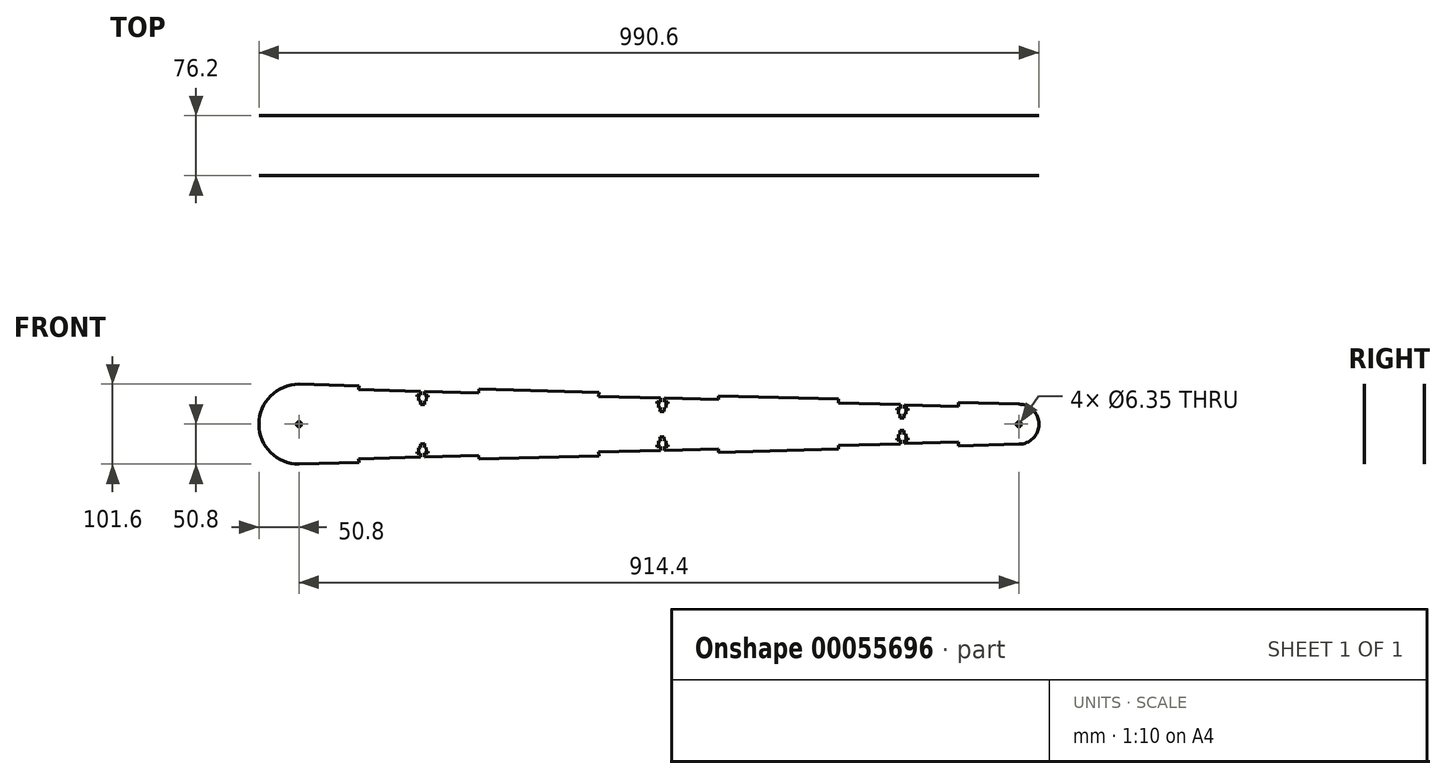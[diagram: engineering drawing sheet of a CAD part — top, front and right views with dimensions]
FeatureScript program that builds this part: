
annotation { "Feature Type Name" : "Feature", "Feature Type Description" : "" }
export const myFeature = defineFeature(function(context is Context, id is Id, definition is map)
    precondition{}
    {
        {
            assignVariable(context, id + "F0", {"name" : "thick", "anyValue" : .188});
        }
        {
            var Q0;
            Q0=qCreatedBy(makeId("Front.planeOp"),FACE);
            var sketch = newSketch(context, id + "F1", { "sketchPlane" : qUnion([Q0])});
            skLineSegment(sketch, "E0", {"start": v(0, 50.8) * mm, "end": v(914.4, 25.4) * mm});
            skLineSegment(sketch, "E1", {"start": v(0, -50.8) * mm, "end": v(914.4, -25.4) * mm});
            skArc(sketch, "E2", {"start": v(0, 50.8) * mm, "mid": v(-50.8, 0) * mm, "end": v(0, -50.8) * mm});
            skLineSegment(sketch, "E3", {"start": v(0, 0) * mm, "end": v(914.4, 0) * mm, "construction": true});
            skArc(sketch, "E4", {"start": v(914.4, 25.4) * mm, "mid": v(939.8, 0) * mm, "end": v(914.4, -25.4) * mm});
            skLineSegment(sketch, "E5", {"start": v(76.17, 48.68) * mm, "end": v(76.04, 43.91) * mm});
            skLineSegment(sketch, "E6", {"start": v(76.04, 43.91) * mm, "end": v(228.38, 39.68) * mm});
            skLineSegment(sketch, "E7", {"start": v(228.38, 39.68) * mm, "end": v(228.51, 44.45) * mm});
            skLineSegment(sketch, "E8", {"start": v(76.17, -48.68) * mm, "end": v(76.04, -43.91) * mm});
            skLineSegment(sketch, "E9", {"start": v(76.04, -43.91) * mm, "end": v(228.38, -39.68) * mm});
            skLineSegment(sketch, "E10", {"start": v(228.38, -39.68) * mm, "end": v(228.51, -44.45) * mm});
            skCircle(sketch, "E11", {"center": v(0, 0) * mm, "radius": 3.17 * mm});
            skCircle(sketch, "E12", {"center": v(914.4, 0) * mm, "radius": 3.18 * mm});
            skLineSegment(sketch, "E13", {"start": v(157.22, 41.66) * mm, "end": v(156.06, 0) * mm, "construction": true});
            skLineSegment(sketch, "E14", {"start": v(154.67, 41.73) * mm, "end": v(154.54, 36.95) * mm});
            skLineSegment(sketch, "E15", {"start": v(154.54, 36.95) * mm, "end": v(150.1, 37.08) * mm});
            skLineSegment(sketch, "E16", {"start": v(150.1, 37.08) * mm, "end": v(150.05, 35.05) * mm});
            skLineSegment(sketch, "E17", {"start": v(150.05, 35.05) * mm, "end": v(152.27, 34.98) * mm});
            skLineSegment(sketch, "E18", {"start": v(152.27, 34.98) * mm, "end": v(152.13, 29.9) * mm});
            skLineSegment(sketch, "E19", {"start": v(152.13, 29.9) * mm, "end": v(154.34, 29.84) * mm});
            skLineSegment(sketch, "E20", {"start": v(154.34, 29.84) * mm, "end": v(154.2, 24.92) * mm});
            skLineSegment(sketch, "E21", {"start": v(154.2, 24.92) * mm, "end": v(156.75, 24.85) * mm});
            skLineSegment(sketch, "E22.MirrorCS", {"start": v(159.77, 41.58) * mm, "end": v(159.64, 36.81) * mm});
            skLineSegment(sketch, "E23.MirrorCS", {"start": v(159.64, 36.81) * mm, "end": v(164.07, 36.69) * mm});
            skLineSegment(sketch, "E24.MirrorCS", {"start": v(164.07, 36.69) * mm, "end": v(164.02, 34.66) * mm});
            skLineSegment(sketch, "E25.MirrorCS", {"start": v(164.02, 34.66) * mm, "end": v(161.8, 34.72) * mm});
            skLineSegment(sketch, "E26.MirrorCS", {"start": v(161.8, 34.72) * mm, "end": v(161.65, 29.64) * mm});
            skLineSegment(sketch, "E27.MirrorCS", {"start": v(161.65, 29.64) * mm, "end": v(159.44, 29.7) * mm});
            skLineSegment(sketch, "E28.MirrorCS", {"start": v(159.44, 29.7) * mm, "end": v(159.3, 24.78) * mm});
            skLineSegment(sketch, "E29.MirrorCS", {"start": v(159.3, 24.78) * mm, "end": v(156.75, 24.85) * mm});
            skLineSegment(sketch, "E30", {"start": v(76.04, -43.91) * mm, "end": v(228.38, 39.68) * mm, "construction": true});
            skLineSegment(sketch, "E31", {"start": v(228.38, -39.68) * mm, "end": v(76.04, 43.91) * mm, "construction": true});
            skLineSegment(sketch, "E32.MirrorCS", {"start": v(159.64, -36.81) * mm, "end": v(164.07, -36.69) * mm});
            skLineSegment(sketch, "E33.MirrorCS", {"start": v(161.65, -29.64) * mm, "end": v(159.44, -29.7) * mm});
            skLineSegment(sketch, "E34.MirrorCS", {"start": v(152.13, -29.9) * mm, "end": v(154.34, -29.84) * mm});
            skLineSegment(sketch, "E35.MirrorCS", {"start": v(159.3, -24.78) * mm, "end": v(156.75, -24.85) * mm});
            skLineSegment(sketch, "E36.MirrorCS", {"start": v(154.2, -24.92) * mm, "end": v(156.75, -24.85) * mm});
            skLineSegment(sketch, "E37.MirrorCS", {"start": v(154.54, -36.95) * mm, "end": v(150.1, -37.08) * mm});
            skLineSegment(sketch, "E38.MirrorCS", {"start": v(164.07, -36.69) * mm, "end": v(164.02, -34.66) * mm});
            skLineSegment(sketch, "E39.MirrorCS", {"start": v(154.34, -29.84) * mm, "end": v(154.2, -24.92) * mm});
            skLineSegment(sketch, "E40.MirrorCS", {"start": v(161.8, -34.72) * mm, "end": v(161.65, -29.64) * mm});
            skLineSegment(sketch, "E41.MirrorCS", {"start": v(150.1, -37.08) * mm, "end": v(150.05, -35.05) * mm});
            skLineSegment(sketch, "E42.MirrorCS", {"start": v(159.77, -41.58) * mm, "end": v(159.64, -36.81) * mm});
            skLineSegment(sketch, "E43.MirrorCS", {"start": v(159.44, -29.7) * mm, "end": v(159.3, -24.78) * mm});
            skLineSegment(sketch, "E44.MirrorCS", {"start": v(152.27, -34.98) * mm, "end": v(152.13, -29.9) * mm});
            skLineSegment(sketch, "E45.MirrorCS", {"start": v(154.67, -41.73) * mm, "end": v(154.54, -36.95) * mm});
            skLineSegment(sketch, "E46.1.0.0", {"start": v(380.72, 35.45) * mm, "end": v(533.06, 31.22) * mm});
            skLineSegment(sketch, "E46.1.0.1", {"start": v(380.85, 40.22) * mm, "end": v(380.72, 35.45) * mm});
            skLineSegment(sketch, "E46.1.0.2", {"start": v(464.46, 33.12) * mm, "end": v(464.32, 28.35) * mm});
            skLineSegment(sketch, "E46.1.0.3", {"start": v(466.48, 26.26) * mm, "end": v(466.33, 21.18) * mm});
            skLineSegment(sketch, "E46.1.0.4", {"start": v(459.35, 33.26) * mm, "end": v(459.22, 28.49) * mm});
            skLineSegment(sketch, "E46.1.0.5", {"start": v(464.13, 21.24) * mm, "end": v(463.99, 16.31) * mm});
            skLineSegment(sketch, "E46.1.0.6", {"start": v(533.06, 31.22) * mm, "end": v(533.2, 35.99) * mm});
            skLineSegment(sketch, "E46.1.0.7", {"start": v(459.02, 21.38) * mm, "end": v(458.89, 16.45) * mm});
            skLineSegment(sketch, "E46.1.0.8", {"start": v(463.99, 16.31) * mm, "end": v(461.44, 16.38) * mm});
            skLineSegment(sketch, "E46.1.0.9", {"start": v(456.81, 21.44) * mm, "end": v(459.02, 21.38) * mm});
            skLineSegment(sketch, "E46.1.0.10", {"start": v(464.32, 28.35) * mm, "end": v(468.75, 28.22) * mm});
            skLineSegment(sketch, "E46.1.0.11", {"start": v(466.33, 21.18) * mm, "end": v(464.13, 21.24) * mm});
            skLineSegment(sketch, "E46.1.0.12", {"start": v(456.95, 26.52) * mm, "end": v(456.81, 21.44) * mm});
            skLineSegment(sketch, "E46.1.0.13", {"start": v(458.89, 16.45) * mm, "end": v(461.44, 16.38) * mm});
            skLineSegment(sketch, "E46.1.0.14", {"start": v(468.7, 26.2) * mm, "end": v(466.48, 26.26) * mm});
            skLineSegment(sketch, "E46.1.0.15", {"start": v(468.75, 28.22) * mm, "end": v(468.7, 26.2) * mm});
            skLineSegment(sketch, "E46.1.0.16", {"start": v(459.22, 28.49) * mm, "end": v(454.79, 28.61) * mm});
            skLineSegment(sketch, "E46.1.0.17", {"start": v(454.79, 28.61) * mm, "end": v(454.73, 26.58) * mm});
            skLineSegment(sketch, "E46.2.0.0", {"start": v(685.4, 26.98) * mm, "end": v(837.74, 22.75) * mm});
            skLineSegment(sketch, "E46.2.0.1", {"start": v(685.54, 31.76) * mm, "end": v(685.4, 26.98) * mm});
            skLineSegment(sketch, "E46.2.0.2", {"start": v(769.14, 24.66) * mm, "end": v(769, 19.88) * mm});
            skLineSegment(sketch, "E46.2.0.3", {"start": v(771.16, 17.8) * mm, "end": v(771.02, 12.71) * mm});
            skLineSegment(sketch, "E46.2.0.4", {"start": v(764.04, 24.8) * mm, "end": v(763.9, 20.03) * mm});
            skLineSegment(sketch, "E46.2.0.5", {"start": v(768.8, 12.78) * mm, "end": v(768.67, 7.85) * mm});
            skLineSegment(sketch, "E46.2.0.6", {"start": v(837.74, 22.75) * mm, "end": v(837.88, 27.53) * mm});
            skLineSegment(sketch, "E46.2.0.7", {"start": v(763.7, 12.92) * mm, "end": v(763.57, 8) * mm});
            skLineSegment(sketch, "E46.2.0.8", {"start": v(768.67, 7.85) * mm, "end": v(766.12, 7.92) * mm});
            skLineSegment(sketch, "E46.2.0.9", {"start": v(761.5, 12.98) * mm, "end": v(763.7, 12.92) * mm});
            skLineSegment(sketch, "E46.2.0.10", {"start": v(769, 19.88) * mm, "end": v(773.44, 19.76) * mm});
            skLineSegment(sketch, "E46.2.0.11", {"start": v(771.02, 12.71) * mm, "end": v(768.8, 12.78) * mm});
            skLineSegment(sketch, "E46.2.0.12", {"start": v(761.64, 18.06) * mm, "end": v(761.5, 12.98) * mm});
            skLineSegment(sketch, "E46.2.0.13", {"start": v(763.57, 8) * mm, "end": v(766.12, 7.92) * mm});
            skLineSegment(sketch, "E46.2.0.14", {"start": v(773.38, 17.73) * mm, "end": v(771.16, 17.8) * mm});
            skLineSegment(sketch, "E46.2.0.15", {"start": v(773.44, 19.76) * mm, "end": v(773.38, 17.73) * mm});
            skLineSegment(sketch, "E46.2.0.16", {"start": v(763.9, 20.03) * mm, "end": v(759.47, 20.15) * mm});
            skLineSegment(sketch, "E46.2.0.17", {"start": v(759.47, 20.15) * mm, "end": v(759.42, 18.12) * mm});
            skLineSegment(sketch, "E46.direction1", {"start": v(76.04, 43.91) * mm, "end": v(380.72, 35.45) * mm, "construction": true});
            skLineSegment(sketch, "E47.1.0.0", {"start": v(464.13, -21.24) * mm, "end": v(463.99, -16.31) * mm});
            skLineSegment(sketch, "E47.1.0.1", {"start": v(459.02, -21.38) * mm, "end": v(458.89, -16.45) * mm});
            skLineSegment(sketch, "E47.1.0.2", {"start": v(466.48, -26.26) * mm, "end": v(466.33, -21.18) * mm});
            skLineSegment(sketch, "E47.1.0.3", {"start": v(380.85, -40.22) * mm, "end": v(380.72, -35.45) * mm});
            skLineSegment(sketch, "E47.1.0.4", {"start": v(533.06, -31.22) * mm, "end": v(533.2, -35.99) * mm});
            skLineSegment(sketch, "E47.1.0.5", {"start": v(380.72, -35.45) * mm, "end": v(533.06, -31.22) * mm});
            skLineSegment(sketch, "E47.1.0.6", {"start": v(464.46, -33.12) * mm, "end": v(464.32, -28.35) * mm});
            skLineSegment(sketch, "E47.1.0.7", {"start": v(459.35, -33.26) * mm, "end": v(459.22, -28.49) * mm});
            skLineSegment(sketch, "E47.1.0.8", {"start": v(456.95, -26.52) * mm, "end": v(456.81, -21.44) * mm});
            skLineSegment(sketch, "E47.1.0.9", {"start": v(463.99, -16.31) * mm, "end": v(461.44, -16.38) * mm});
            skLineSegment(sketch, "E47.1.0.10", {"start": v(454.79, -28.61) * mm, "end": v(454.73, -26.58) * mm});
            skLineSegment(sketch, "E47.1.0.11", {"start": v(464.32, -28.35) * mm, "end": v(468.75, -28.22) * mm});
            skLineSegment(sketch, "E47.1.0.12", {"start": v(468.75, -28.22) * mm, "end": v(468.7, -26.2) * mm});
            skLineSegment(sketch, "E47.1.0.13", {"start": v(466.33, -21.18) * mm, "end": v(464.13, -21.24) * mm});
            skLineSegment(sketch, "E47.1.0.14", {"start": v(459.22, -28.49) * mm, "end": v(454.79, -28.61) * mm});
            skLineSegment(sketch, "E47.1.0.15", {"start": v(456.81, -21.44) * mm, "end": v(459.02, -21.38) * mm});
            skLineSegment(sketch, "E47.1.0.16", {"start": v(458.89, -16.45) * mm, "end": v(461.44, -16.38) * mm});
            skLineSegment(sketch, "E47.2.0.0", {"start": v(768.8, -12.78) * mm, "end": v(768.67, -7.85) * mm});
            skLineSegment(sketch, "E47.2.0.1", {"start": v(763.7, -12.92) * mm, "end": v(763.57, -8) * mm});
            skLineSegment(sketch, "E47.2.0.2", {"start": v(771.16, -17.8) * mm, "end": v(771.02, -12.71) * mm});
            skLineSegment(sketch, "E47.2.0.3", {"start": v(685.54, -31.76) * mm, "end": v(685.4, -26.98) * mm});
            skLineSegment(sketch, "E47.2.0.4", {"start": v(837.74, -22.75) * mm, "end": v(837.88, -27.53) * mm});
            skLineSegment(sketch, "E47.2.0.5", {"start": v(685.4, -26.98) * mm, "end": v(837.74, -22.75) * mm});
            skLineSegment(sketch, "E47.2.0.6", {"start": v(769.14, -24.66) * mm, "end": v(769, -19.88) * mm});
            skLineSegment(sketch, "E47.2.0.7", {"start": v(764.04, -24.8) * mm, "end": v(763.9, -20.03) * mm});
            skLineSegment(sketch, "E47.2.0.8", {"start": v(761.64, -18.06) * mm, "end": v(761.5, -12.98) * mm});
            skLineSegment(sketch, "E47.2.0.9", {"start": v(768.67, -7.85) * mm, "end": v(766.12, -7.92) * mm});
            skLineSegment(sketch, "E47.2.0.10", {"start": v(759.47, -20.15) * mm, "end": v(759.42, -18.12) * mm});
            skLineSegment(sketch, "E47.2.0.11", {"start": v(769, -19.88) * mm, "end": v(773.44, -19.76) * mm});
            skLineSegment(sketch, "E47.2.0.12", {"start": v(773.44, -19.76) * mm, "end": v(773.38, -17.73) * mm});
            skLineSegment(sketch, "E47.2.0.13", {"start": v(771.02, -12.71) * mm, "end": v(768.8, -12.78) * mm});
            skLineSegment(sketch, "E47.2.0.14", {"start": v(763.9, -20.03) * mm, "end": v(759.47, -20.15) * mm});
            skLineSegment(sketch, "E47.2.0.15", {"start": v(761.5, -12.98) * mm, "end": v(763.7, -12.92) * mm});
            skLineSegment(sketch, "E47.2.0.16", {"start": v(763.57, -8) * mm, "end": v(766.12, -7.92) * mm});
            skLineSegment(sketch, "E47.direction1", {"start": v(159.44, -29.7) * mm, "end": v(464.13, -21.24) * mm, "construction": true});
            skLineSegment(sketch, "E48", {"start": v(150.05, -35.05) * mm, "end": v(152.27, -34.98) * mm});
            skLineSegment(sketch, "E49", {"start": v(161.8, -34.72) * mm, "end": v(164.02, -34.66) * mm});
            skLineSegment(sketch, "E50", {"start": v(454.73, 26.58) * mm, "end": v(456.95, 26.52) * mm});
            skLineSegment(sketch, "E51", {"start": v(454.73, -26.58) * mm, "end": v(456.95, -26.52) * mm});
            skLineSegment(sketch, "E52", {"start": v(466.48, -26.26) * mm, "end": v(468.7, -26.2) * mm});
            skLineSegment(sketch, "E53", {"start": v(759.42, 18.12) * mm, "end": v(761.64, 18.06) * mm});
            skLineSegment(sketch, "E54", {"start": v(759.42, -18.12) * mm, "end": v(761.64, -18.06) * mm});
            skLineSegment(sketch, "E55", {"start": v(771.16, -17.8) * mm, "end": v(773.38, -17.73) * mm});
            skSolve(sketch);
        }
        {
            var Q0;
            Q0=qCreatedBy(makeId("Front.planeOp"),FACE);
            cPlane(context, id + "F2", {"entities" : qUnion([Q0]), "cplaneType" : CPlaneType.OFFSET, "offset" : 38.1 * mm, "width" : 152.4 * mm, "height" : 152.4 * mm});
        }
        {
            var Q0;
            Q0=qCreatedBy(makeId("Front.planeOp"),FACE);
            cPlane(context, id + "F3", {"entities" : qUnion([Q0]), "cplaneType" : CPlaneType.OFFSET, "offset" : 38.1 * mm, "oppositeDirection" : true, "width" : 152.4 * mm, "height" : 152.4 * mm});
        }
        {
            var Q0;
            Q0=qCreatedBy(id+"F2.planeOp",FACE);
            var sketch = newSketch(context, id + "F4", { "sketchPlane" : qUnion([Q0])});
            skLineSegment(sketch, "E56.0.0", {"start": v(76.17, 48.68) * mm, "end": v(0, 50.8) * mm});
            skArc(sketch, "E56.0.1", {"start": v(0, 50.8) * mm, "mid": v(-50.8, 0) * mm, "end": v(0, -50.8) * mm});
            skLineSegment(sketch, "E56.0.2", {"start": v(0, -50.8) * mm, "end": v(76.17, -48.68) * mm});
            skLineSegment(sketch, "E56.0.3", {"start": v(76.17, -48.68) * mm, "end": v(76.04, -43.91) * mm});
            skLineSegment(sketch, "E56.0.4", {"start": v(76.04, -43.91) * mm, "end": v(154.67, -41.73) * mm});
            skLineSegment(sketch, "E56.0.5", {"start": v(154.67, -41.73) * mm, "end": v(154.54, -36.95) * mm});
            skLineSegment(sketch, "E56.0.6", {"start": v(154.54, -36.95) * mm, "end": v(150.1, -37.08) * mm});
            skLineSegment(sketch, "E56.0.7", {"start": v(150.1, -37.08) * mm, "end": v(150.05, -35.05) * mm});
            skLineSegment(sketch, "E56.0.8", {"start": v(150.05, -35.05) * mm, "end": v(152.27, -34.98) * mm});
            skLineSegment(sketch, "E56.0.9", {"start": v(152.27, -34.98) * mm, "end": v(152.13, -29.9) * mm});
            skLineSegment(sketch, "E56.0.10", {"start": v(152.13, -29.9) * mm, "end": v(154.34, -29.84) * mm});
            skLineSegment(sketch, "E56.0.11", {"start": v(154.34, -29.84) * mm, "end": v(154.2, -24.92) * mm});
            skLineSegment(sketch, "E56.0.12", {"start": v(154.2, -24.92) * mm, "end": v(156.75, -24.85) * mm});
            skLineSegment(sketch, "E56.0.13", {"start": v(156.75, -24.85) * mm, "end": v(159.3, -24.78) * mm});
            skLineSegment(sketch, "E56.0.14", {"start": v(159.3, -24.78) * mm, "end": v(159.44, -29.7) * mm});
            skLineSegment(sketch, "E56.0.15", {"start": v(159.44, -29.7) * mm, "end": v(161.65, -29.64) * mm});
            skLineSegment(sketch, "E56.0.16", {"start": v(161.65, -29.64) * mm, "end": v(161.8, -34.72) * mm});
            skLineSegment(sketch, "E56.0.17", {"start": v(161.8, -34.72) * mm, "end": v(164.02, -34.66) * mm});
            skLineSegment(sketch, "E56.0.18", {"start": v(164.02, -34.66) * mm, "end": v(164.07, -36.69) * mm});
            skLineSegment(sketch, "E56.0.19", {"start": v(164.07, -36.69) * mm, "end": v(159.64, -36.81) * mm});
            skLineSegment(sketch, "E56.0.20", {"start": v(159.64, -36.81) * mm, "end": v(159.77, -41.58) * mm});
            skLineSegment(sketch, "E56.0.21", {"start": v(159.77, -41.58) * mm, "end": v(228.38, -39.68) * mm});
            skLineSegment(sketch, "E56.0.22", {"start": v(228.38, -39.68) * mm, "end": v(228.51, -44.45) * mm});
            skLineSegment(sketch, "E56.0.23", {"start": v(228.51, -44.45) * mm, "end": v(380.85, -40.22) * mm});
            skLineSegment(sketch, "E56.0.24", {"start": v(380.85, -40.22) * mm, "end": v(380.72, -35.45) * mm});
            skLineSegment(sketch, "E56.0.25", {"start": v(380.72, -35.45) * mm, "end": v(459.35, -33.26) * mm});
            skLineSegment(sketch, "E56.0.26", {"start": v(459.35, -33.26) * mm, "end": v(459.22, -28.49) * mm});
            skLineSegment(sketch, "E56.0.27", {"start": v(459.22, -28.49) * mm, "end": v(454.79, -28.61) * mm});
            skLineSegment(sketch, "E56.0.28", {"start": v(454.79, -28.61) * mm, "end": v(454.73, -26.58) * mm});
            skLineSegment(sketch, "E56.0.29", {"start": v(454.73, -26.58) * mm, "end": v(456.95, -26.52) * mm});
            skLineSegment(sketch, "E56.0.30", {"start": v(456.95, -26.52) * mm, "end": v(456.81, -21.44) * mm});
            skLineSegment(sketch, "E56.0.31", {"start": v(456.81, -21.44) * mm, "end": v(459.02, -21.38) * mm});
            skLineSegment(sketch, "E56.0.32", {"start": v(459.02, -21.38) * mm, "end": v(458.89, -16.45) * mm});
            skLineSegment(sketch, "E56.0.33", {"start": v(458.89, -16.45) * mm, "end": v(461.44, -16.38) * mm});
            skLineSegment(sketch, "E56.0.34", {"start": v(461.44, -16.38) * mm, "end": v(463.99, -16.31) * mm});
            skLineSegment(sketch, "E56.0.35", {"start": v(463.99, -16.31) * mm, "end": v(464.13, -21.24) * mm});
            skLineSegment(sketch, "E56.0.36", {"start": v(464.13, -21.24) * mm, "end": v(466.33, -21.18) * mm});
            skLineSegment(sketch, "E56.0.37", {"start": v(466.33, -21.18) * mm, "end": v(466.48, -26.26) * mm});
            skLineSegment(sketch, "E56.0.38", {"start": v(466.48, -26.26) * mm, "end": v(468.7, -26.2) * mm});
            skLineSegment(sketch, "E56.0.39", {"start": v(468.7, -26.2) * mm, "end": v(468.75, -28.22) * mm});
            skLineSegment(sketch, "E56.0.40", {"start": v(468.75, -28.22) * mm, "end": v(464.32, -28.35) * mm});
            skLineSegment(sketch, "E56.0.41", {"start": v(464.32, -28.35) * mm, "end": v(464.46, -33.12) * mm});
            skLineSegment(sketch, "E56.0.42", {"start": v(464.46, -33.12) * mm, "end": v(533.06, -31.22) * mm});
            skLineSegment(sketch, "E56.0.43", {"start": v(533.06, -31.22) * mm, "end": v(533.2, -35.99) * mm});
            skLineSegment(sketch, "E56.0.44", {"start": v(533.2, -35.99) * mm, "end": v(685.54, -31.76) * mm});
            skLineSegment(sketch, "E56.0.45", {"start": v(685.54, -31.76) * mm, "end": v(685.4, -26.98) * mm});
            skLineSegment(sketch, "E56.0.46", {"start": v(685.4, -26.98) * mm, "end": v(764.04, -24.8) * mm});
            skLineSegment(sketch, "E56.0.47", {"start": v(764.04, -24.8) * mm, "end": v(763.9, -20.03) * mm});
            skLineSegment(sketch, "E56.0.48", {"start": v(763.9, -20.03) * mm, "end": v(759.47, -20.15) * mm});
            skLineSegment(sketch, "E56.0.49", {"start": v(759.47, -20.15) * mm, "end": v(759.42, -18.12) * mm});
            skLineSegment(sketch, "E56.0.50", {"start": v(759.42, -18.12) * mm, "end": v(761.64, -18.06) * mm});
            skLineSegment(sketch, "E56.0.51", {"start": v(761.64, -18.06) * mm, "end": v(761.5, -12.98) * mm});
            skLineSegment(sketch, "E56.0.52", {"start": v(761.5, -12.98) * mm, "end": v(763.7, -12.92) * mm});
            skLineSegment(sketch, "E56.0.53", {"start": v(763.7, -12.92) * mm, "end": v(763.57, -8) * mm});
            skLineSegment(sketch, "E56.0.54", {"start": v(763.57, -8) * mm, "end": v(766.12, -7.92) * mm});
            skLineSegment(sketch, "E56.0.55", {"start": v(766.12, -7.92) * mm, "end": v(768.67, -7.85) * mm});
            skLineSegment(sketch, "E56.0.56", {"start": v(768.67, -7.85) * mm, "end": v(768.8, -12.78) * mm});
            skLineSegment(sketch, "E56.0.57", {"start": v(768.8, -12.78) * mm, "end": v(771.02, -12.71) * mm});
            skLineSegment(sketch, "E56.0.58", {"start": v(771.02, -12.71) * mm, "end": v(771.16, -17.8) * mm});
            skLineSegment(sketch, "E56.0.59", {"start": v(771.16, -17.8) * mm, "end": v(773.38, -17.73) * mm});
            skLineSegment(sketch, "E56.0.60", {"start": v(773.38, -17.73) * mm, "end": v(773.44, -19.76) * mm});
            skLineSegment(sketch, "E56.0.61", {"start": v(773.44, -19.76) * mm, "end": v(769, -19.88) * mm});
            skLineSegment(sketch, "E56.0.62", {"start": v(769, -19.88) * mm, "end": v(769.14, -24.66) * mm});
            skLineSegment(sketch, "E56.0.63", {"start": v(769.14, -24.66) * mm, "end": v(837.74, -22.75) * mm});
            skLineSegment(sketch, "E56.0.64", {"start": v(837.74, -22.75) * mm, "end": v(837.88, -27.53) * mm});
            skLineSegment(sketch, "E56.0.65", {"start": v(837.88, -27.53) * mm, "end": v(914.4, -25.4) * mm});
            skArc(sketch, "E56.0.66", {"start": v(914.4, -25.4) * mm, "mid": v(939.8, 0) * mm, "end": v(914.4, 25.4) * mm});
            skLineSegment(sketch, "E56.0.67", {"start": v(914.4, 25.4) * mm, "end": v(837.88, 27.53) * mm});
            skLineSegment(sketch, "E56.0.68", {"start": v(837.88, 27.53) * mm, "end": v(837.74, 22.75) * mm});
            skLineSegment(sketch, "E56.0.69", {"start": v(837.74, 22.75) * mm, "end": v(769.14, 24.66) * mm});
            skLineSegment(sketch, "E56.0.70", {"start": v(769.14, 24.66) * mm, "end": v(769, 19.88) * mm});
            skLineSegment(sketch, "E56.0.71", {"start": v(769, 19.88) * mm, "end": v(773.44, 19.76) * mm});
            skLineSegment(sketch, "E56.0.72", {"start": v(773.44, 19.76) * mm, "end": v(773.38, 17.73) * mm});
            skLineSegment(sketch, "E56.0.73", {"start": v(773.38, 17.73) * mm, "end": v(771.16, 17.8) * mm});
            skLineSegment(sketch, "E56.0.74", {"start": v(771.16, 17.8) * mm, "end": v(771.02, 12.71) * mm});
            skLineSegment(sketch, "E56.0.75", {"start": v(771.02, 12.71) * mm, "end": v(768.8, 12.78) * mm});
            skLineSegment(sketch, "E56.0.76", {"start": v(768.8, 12.78) * mm, "end": v(768.67, 7.85) * mm});
            skLineSegment(sketch, "E56.0.77", {"start": v(768.67, 7.85) * mm, "end": v(766.12, 7.92) * mm});
            skLineSegment(sketch, "E56.0.78", {"start": v(766.12, 7.92) * mm, "end": v(763.57, 8) * mm});
            skLineSegment(sketch, "E56.0.79", {"start": v(763.57, 8) * mm, "end": v(763.7, 12.92) * mm});
            skLineSegment(sketch, "E56.0.80", {"start": v(763.7, 12.92) * mm, "end": v(761.5, 12.98) * mm});
            skLineSegment(sketch, "E56.0.81", {"start": v(761.5, 12.98) * mm, "end": v(761.64, 18.06) * mm});
            skLineSegment(sketch, "E56.0.82", {"start": v(761.64, 18.06) * mm, "end": v(759.42, 18.12) * mm});
            skLineSegment(sketch, "E56.0.83", {"start": v(759.42, 18.12) * mm, "end": v(759.47, 20.15) * mm});
            skLineSegment(sketch, "E56.0.84", {"start": v(759.47, 20.15) * mm, "end": v(763.9, 20.03) * mm});
            skLineSegment(sketch, "E56.0.85", {"start": v(763.9, 20.03) * mm, "end": v(764.04, 24.8) * mm});
            skLineSegment(sketch, "E56.0.86", {"start": v(764.04, 24.8) * mm, "end": v(685.4, 26.98) * mm});
            skLineSegment(sketch, "E56.0.87", {"start": v(685.4, 26.98) * mm, "end": v(685.54, 31.76) * mm});
            skLineSegment(sketch, "E56.0.88", {"start": v(685.54, 31.76) * mm, "end": v(533.2, 35.99) * mm});
            skLineSegment(sketch, "E56.0.89", {"start": v(533.2, 35.99) * mm, "end": v(533.06, 31.22) * mm});
            skLineSegment(sketch, "E56.0.90", {"start": v(533.06, 31.22) * mm, "end": v(464.46, 33.12) * mm});
            skLineSegment(sketch, "E56.0.91", {"start": v(464.46, 33.12) * mm, "end": v(464.32, 28.35) * mm});
            skLineSegment(sketch, "E56.0.92", {"start": v(464.32, 28.35) * mm, "end": v(468.75, 28.22) * mm});
            skLineSegment(sketch, "E56.0.93", {"start": v(468.75, 28.22) * mm, "end": v(468.7, 26.2) * mm});
            skLineSegment(sketch, "E56.0.94", {"start": v(468.7, 26.2) * mm, "end": v(466.48, 26.26) * mm});
            skLineSegment(sketch, "E56.0.95", {"start": v(466.48, 26.26) * mm, "end": v(466.33, 21.18) * mm});
            skLineSegment(sketch, "E56.0.96", {"start": v(466.33, 21.18) * mm, "end": v(464.13, 21.24) * mm});
            skLineSegment(sketch, "E56.0.97", {"start": v(464.13, 21.24) * mm, "end": v(463.99, 16.31) * mm});
            skLineSegment(sketch, "E56.0.98", {"start": v(463.99, 16.31) * mm, "end": v(461.44, 16.38) * mm});
            skLineSegment(sketch, "E56.0.99", {"start": v(461.44, 16.38) * mm, "end": v(458.89, 16.45) * mm});
            skLineSegment(sketch, "E56.0.100", {"start": v(458.89, 16.45) * mm, "end": v(459.02, 21.38) * mm});
            skLineSegment(sketch, "E56.0.101", {"start": v(459.02, 21.38) * mm, "end": v(456.81, 21.44) * mm});
            skLineSegment(sketch, "E56.0.102", {"start": v(456.81, 21.44) * mm, "end": v(456.95, 26.52) * mm});
            skLineSegment(sketch, "E56.0.103", {"start": v(456.95, 26.52) * mm, "end": v(454.73, 26.58) * mm});
            skLineSegment(sketch, "E56.0.104", {"start": v(454.73, 26.58) * mm, "end": v(454.79, 28.61) * mm});
            skLineSegment(sketch, "E56.0.105", {"start": v(454.79, 28.61) * mm, "end": v(459.22, 28.49) * mm});
            skLineSegment(sketch, "E56.0.106", {"start": v(459.22, 28.49) * mm, "end": v(459.35, 33.26) * mm});
            skLineSegment(sketch, "E56.0.107", {"start": v(459.35, 33.26) * mm, "end": v(380.72, 35.45) * mm});
            skLineSegment(sketch, "E56.0.108", {"start": v(380.72, 35.45) * mm, "end": v(380.85, 40.22) * mm});
            skLineSegment(sketch, "E56.0.109", {"start": v(380.85, 40.22) * mm, "end": v(228.51, 44.45) * mm});
            skLineSegment(sketch, "E56.0.110", {"start": v(228.51, 44.45) * mm, "end": v(228.38, 39.68) * mm});
            skLineSegment(sketch, "E56.0.111", {"start": v(228.38, 39.68) * mm, "end": v(159.77, 41.58) * mm});
            skLineSegment(sketch, "E56.0.112", {"start": v(159.77, 41.58) * mm, "end": v(159.64, 36.81) * mm});
            skLineSegment(sketch, "E56.0.113", {"start": v(159.64, 36.81) * mm, "end": v(164.07, 36.69) * mm});
            skLineSegment(sketch, "E56.0.114", {"start": v(164.07, 36.69) * mm, "end": v(164.02, 34.66) * mm});
            skLineSegment(sketch, "E56.0.115", {"start": v(164.02, 34.66) * mm, "end": v(161.8, 34.72) * mm});
            skLineSegment(sketch, "E56.0.116", {"start": v(161.8, 34.72) * mm, "end": v(161.65, 29.64) * mm});
            skLineSegment(sketch, "E56.0.117", {"start": v(161.65, 29.64) * mm, "end": v(159.44, 29.7) * mm});
            skLineSegment(sketch, "E56.0.118", {"start": v(159.44, 29.7) * mm, "end": v(159.3, 24.78) * mm});
            skLineSegment(sketch, "E56.0.119", {"start": v(159.3, 24.78) * mm, "end": v(156.75, 24.85) * mm});
            skLineSegment(sketch, "E56.0.120", {"start": v(156.75, 24.85) * mm, "end": v(154.2, 24.92) * mm});
            skLineSegment(sketch, "E56.0.121", {"start": v(154.2, 24.92) * mm, "end": v(154.34, 29.84) * mm});
            skLineSegment(sketch, "E56.0.122", {"start": v(154.34, 29.84) * mm, "end": v(152.13, 29.9) * mm});
            skLineSegment(sketch, "E56.0.123", {"start": v(152.13, 29.9) * mm, "end": v(152.27, 34.98) * mm});
            skLineSegment(sketch, "E56.0.124", {"start": v(152.27, 34.98) * mm, "end": v(150.05, 35.05) * mm});
            skLineSegment(sketch, "E56.0.125", {"start": v(150.05, 35.05) * mm, "end": v(150.1, 37.08) * mm});
            skLineSegment(sketch, "E56.0.126", {"start": v(150.1, 37.08) * mm, "end": v(154.54, 36.95) * mm});
            skLineSegment(sketch, "E56.0.127", {"start": v(154.54, 36.95) * mm, "end": v(154.67, 41.73) * mm});
            skLineSegment(sketch, "E56.0.128", {"start": v(154.67, 41.73) * mm, "end": v(76.04, 43.91) * mm});
            skLineSegment(sketch, "E56.0.129", {"start": v(76.04, 43.91) * mm, "end": v(76.17, 48.68) * mm});
            skCircle(sketch, "E57.0", {"center": v(0, 0) * mm, "radius": 3.17 * mm});
            skCircle(sketch, "E58.0", {"center": v(914.4, 0) * mm, "radius": 3.18 * mm});
            skSolve(sketch);
        }
        {
            var Q0;
            Q0 = qSketchRegion(id + "F4", true);
            extrude(context, id + "F5", {"entities" : qUnion([Q0]), "oppositeDirection" : true, "depth" : (getVariable(context, 'thick')) * mm});
        }
        {
            var Q0;
            Q0=qCreatedBy(id+"F3.planeOp",FACE);
            var sketch = newSketch(context, id + "F6", { "sketchPlane" : qUnion([Q0])});
            skLineSegment(sketch, "E59.0.0", {"start": v(76.17, 48.68) * mm, "end": v(0, 50.8) * mm});
            skArc(sketch, "E59.0.1", {"start": v(0, 50.8) * mm, "mid": v(-50.8, 0) * mm, "end": v(0, -50.8) * mm});
            skLineSegment(sketch, "E59.0.2", {"start": v(0, -50.8) * mm, "end": v(76.17, -48.68) * mm});
            skLineSegment(sketch, "E59.0.3", {"start": v(76.17, -48.68) * mm, "end": v(76.04, -43.91) * mm});
            skLineSegment(sketch, "E59.0.4", {"start": v(76.04, -43.91) * mm, "end": v(154.67, -41.73) * mm});
            skLineSegment(sketch, "E59.0.5", {"start": v(154.67, -41.73) * mm, "end": v(154.54, -36.95) * mm});
            skLineSegment(sketch, "E59.0.6", {"start": v(154.54, -36.95) * mm, "end": v(150.1, -37.08) * mm});
            skLineSegment(sketch, "E59.0.7", {"start": v(150.1, -37.08) * mm, "end": v(150.05, -35.05) * mm});
            skLineSegment(sketch, "E59.0.8", {"start": v(150.05, -35.05) * mm, "end": v(152.27, -34.98) * mm});
            skLineSegment(sketch, "E59.0.9", {"start": v(152.27, -34.98) * mm, "end": v(152.13, -29.9) * mm});
            skLineSegment(sketch, "E59.0.10", {"start": v(152.13, -29.9) * mm, "end": v(154.34, -29.84) * mm});
            skLineSegment(sketch, "E59.0.11", {"start": v(154.34, -29.84) * mm, "end": v(154.2, -24.92) * mm});
            skLineSegment(sketch, "E59.0.12", {"start": v(154.2, -24.92) * mm, "end": v(156.75, -24.85) * mm});
            skLineSegment(sketch, "E59.0.13", {"start": v(156.75, -24.85) * mm, "end": v(159.3, -24.78) * mm});
            skLineSegment(sketch, "E59.0.14", {"start": v(159.3, -24.78) * mm, "end": v(159.44, -29.7) * mm});
            skLineSegment(sketch, "E59.0.15", {"start": v(159.44, -29.7) * mm, "end": v(161.65, -29.64) * mm});
            skLineSegment(sketch, "E59.0.16", {"start": v(161.65, -29.64) * mm, "end": v(161.8, -34.72) * mm});
            skLineSegment(sketch, "E59.0.17", {"start": v(161.8, -34.72) * mm, "end": v(164.02, -34.66) * mm});
            skLineSegment(sketch, "E59.0.18", {"start": v(164.02, -34.66) * mm, "end": v(164.07, -36.69) * mm});
            skLineSegment(sketch, "E59.0.19", {"start": v(164.07, -36.69) * mm, "end": v(159.64, -36.81) * mm});
            skLineSegment(sketch, "E59.0.20", {"start": v(159.64, -36.81) * mm, "end": v(159.77, -41.58) * mm});
            skLineSegment(sketch, "E59.0.21", {"start": v(159.77, -41.58) * mm, "end": v(228.38, -39.68) * mm});
            skLineSegment(sketch, "E59.0.22", {"start": v(228.38, -39.68) * mm, "end": v(228.51, -44.45) * mm});
            skLineSegment(sketch, "E59.0.23", {"start": v(228.51, -44.45) * mm, "end": v(380.85, -40.22) * mm});
            skLineSegment(sketch, "E59.0.24", {"start": v(380.85, -40.22) * mm, "end": v(380.72, -35.45) * mm});
            skLineSegment(sketch, "E59.0.25", {"start": v(380.72, -35.45) * mm, "end": v(459.35, -33.26) * mm});
            skLineSegment(sketch, "E59.0.26", {"start": v(459.35, -33.26) * mm, "end": v(459.22, -28.49) * mm});
            skLineSegment(sketch, "E59.0.27", {"start": v(459.22, -28.49) * mm, "end": v(454.79, -28.61) * mm});
            skLineSegment(sketch, "E59.0.28", {"start": v(454.79, -28.61) * mm, "end": v(454.73, -26.58) * mm});
            skLineSegment(sketch, "E59.0.29", {"start": v(454.73, -26.58) * mm, "end": v(456.95, -26.52) * mm});
            skLineSegment(sketch, "E59.0.30", {"start": v(456.95, -26.52) * mm, "end": v(456.81, -21.44) * mm});
            skLineSegment(sketch, "E59.0.31", {"start": v(456.81, -21.44) * mm, "end": v(459.02, -21.38) * mm});
            skLineSegment(sketch, "E59.0.32", {"start": v(459.02, -21.38) * mm, "end": v(458.89, -16.45) * mm});
            skLineSegment(sketch, "E59.0.33", {"start": v(458.89, -16.45) * mm, "end": v(461.44, -16.38) * mm});
            skLineSegment(sketch, "E59.0.34", {"start": v(461.44, -16.38) * mm, "end": v(463.99, -16.31) * mm});
            skLineSegment(sketch, "E59.0.35", {"start": v(463.99, -16.31) * mm, "end": v(464.13, -21.24) * mm});
            skLineSegment(sketch, "E59.0.36", {"start": v(464.13, -21.24) * mm, "end": v(466.33, -21.18) * mm});
            skLineSegment(sketch, "E59.0.37", {"start": v(466.33, -21.18) * mm, "end": v(466.48, -26.26) * mm});
            skLineSegment(sketch, "E59.0.38", {"start": v(466.48, -26.26) * mm, "end": v(468.7, -26.2) * mm});
            skLineSegment(sketch, "E59.0.39", {"start": v(468.7, -26.2) * mm, "end": v(468.75, -28.22) * mm});
            skLineSegment(sketch, "E59.0.40", {"start": v(468.75, -28.22) * mm, "end": v(464.32, -28.35) * mm});
            skLineSegment(sketch, "E59.0.41", {"start": v(464.32, -28.35) * mm, "end": v(464.46, -33.12) * mm});
            skLineSegment(sketch, "E59.0.42", {"start": v(464.46, -33.12) * mm, "end": v(533.06, -31.22) * mm});
            skLineSegment(sketch, "E59.0.43", {"start": v(533.06, -31.22) * mm, "end": v(533.2, -35.99) * mm});
            skLineSegment(sketch, "E59.0.44", {"start": v(533.2, -35.99) * mm, "end": v(685.54, -31.76) * mm});
            skLineSegment(sketch, "E59.0.45", {"start": v(685.54, -31.76) * mm, "end": v(685.4, -26.98) * mm});
            skLineSegment(sketch, "E59.0.46", {"start": v(685.4, -26.98) * mm, "end": v(764.04, -24.8) * mm});
            skLineSegment(sketch, "E59.0.47", {"start": v(764.04, -24.8) * mm, "end": v(763.9, -20.03) * mm});
            skLineSegment(sketch, "E59.0.48", {"start": v(763.9, -20.03) * mm, "end": v(759.47, -20.15) * mm});
            skLineSegment(sketch, "E59.0.49", {"start": v(759.47, -20.15) * mm, "end": v(759.42, -18.12) * mm});
            skLineSegment(sketch, "E59.0.50", {"start": v(759.42, -18.12) * mm, "end": v(761.64, -18.06) * mm});
            skLineSegment(sketch, "E59.0.51", {"start": v(761.64, -18.06) * mm, "end": v(761.5, -12.98) * mm});
            skLineSegment(sketch, "E59.0.52", {"start": v(761.5, -12.98) * mm, "end": v(763.7, -12.92) * mm});
            skLineSegment(sketch, "E59.0.53", {"start": v(763.7, -12.92) * mm, "end": v(763.57, -8) * mm});
            skLineSegment(sketch, "E59.0.54", {"start": v(763.57, -8) * mm, "end": v(766.12, -7.92) * mm});
            skLineSegment(sketch, "E59.0.55", {"start": v(766.12, -7.92) * mm, "end": v(768.67, -7.85) * mm});
            skLineSegment(sketch, "E59.0.56", {"start": v(768.67, -7.85) * mm, "end": v(768.8, -12.78) * mm});
            skLineSegment(sketch, "E59.0.57", {"start": v(768.8, -12.78) * mm, "end": v(771.02, -12.71) * mm});
            skLineSegment(sketch, "E59.0.58", {"start": v(771.02, -12.71) * mm, "end": v(771.16, -17.8) * mm});
            skLineSegment(sketch, "E59.0.59", {"start": v(771.16, -17.8) * mm, "end": v(773.38, -17.73) * mm});
            skLineSegment(sketch, "E59.0.60", {"start": v(773.38, -17.73) * mm, "end": v(773.44, -19.76) * mm});
            skLineSegment(sketch, "E59.0.61", {"start": v(773.44, -19.76) * mm, "end": v(769, -19.88) * mm});
            skLineSegment(sketch, "E59.0.62", {"start": v(769, -19.88) * mm, "end": v(769.14, -24.66) * mm});
            skLineSegment(sketch, "E59.0.63", {"start": v(769.14, -24.66) * mm, "end": v(837.74, -22.75) * mm});
            skLineSegment(sketch, "E59.0.64", {"start": v(837.74, -22.75) * mm, "end": v(837.88, -27.53) * mm});
            skLineSegment(sketch, "E59.0.65", {"start": v(837.88, -27.53) * mm, "end": v(914.4, -25.4) * mm});
            skArc(sketch, "E59.0.66", {"start": v(914.4, -25.4) * mm, "mid": v(939.8, 0) * mm, "end": v(914.4, 25.4) * mm});
            skLineSegment(sketch, "E59.0.67", {"start": v(914.4, 25.4) * mm, "end": v(837.88, 27.53) * mm});
            skLineSegment(sketch, "E59.0.68", {"start": v(837.88, 27.53) * mm, "end": v(837.74, 22.75) * mm});
            skLineSegment(sketch, "E59.0.69", {"start": v(837.74, 22.75) * mm, "end": v(769.14, 24.66) * mm});
            skLineSegment(sketch, "E59.0.70", {"start": v(769.14, 24.66) * mm, "end": v(769, 19.88) * mm});
            skLineSegment(sketch, "E59.0.71", {"start": v(769, 19.88) * mm, "end": v(773.44, 19.76) * mm});
            skLineSegment(sketch, "E59.0.72", {"start": v(773.44, 19.76) * mm, "end": v(773.38, 17.73) * mm});
            skLineSegment(sketch, "E59.0.73", {"start": v(773.38, 17.73) * mm, "end": v(771.16, 17.8) * mm});
            skLineSegment(sketch, "E59.0.74", {"start": v(771.16, 17.8) * mm, "end": v(771.02, 12.71) * mm});
            skLineSegment(sketch, "E59.0.75", {"start": v(771.02, 12.71) * mm, "end": v(768.8, 12.78) * mm});
            skLineSegment(sketch, "E59.0.76", {"start": v(768.8, 12.78) * mm, "end": v(768.67, 7.85) * mm});
            skLineSegment(sketch, "E59.0.77", {"start": v(768.67, 7.85) * mm, "end": v(766.12, 7.92) * mm});
            skLineSegment(sketch, "E59.0.78", {"start": v(766.12, 7.92) * mm, "end": v(763.57, 8) * mm});
            skLineSegment(sketch, "E59.0.79", {"start": v(763.57, 8) * mm, "end": v(763.7, 12.92) * mm});
            skLineSegment(sketch, "E59.0.80", {"start": v(763.7, 12.92) * mm, "end": v(761.5, 12.98) * mm});
            skLineSegment(sketch, "E59.0.81", {"start": v(761.5, 12.98) * mm, "end": v(761.64, 18.06) * mm});
            skLineSegment(sketch, "E59.0.82", {"start": v(761.64, 18.06) * mm, "end": v(759.42, 18.12) * mm});
            skLineSegment(sketch, "E59.0.83", {"start": v(759.42, 18.12) * mm, "end": v(759.47, 20.15) * mm});
            skLineSegment(sketch, "E59.0.84", {"start": v(759.47, 20.15) * mm, "end": v(763.9, 20.03) * mm});
            skLineSegment(sketch, "E59.0.85", {"start": v(763.9, 20.03) * mm, "end": v(764.04, 24.8) * mm});
            skLineSegment(sketch, "E59.0.86", {"start": v(764.04, 24.8) * mm, "end": v(685.4, 26.98) * mm});
            skLineSegment(sketch, "E59.0.87", {"start": v(685.4, 26.98) * mm, "end": v(685.54, 31.76) * mm});
            skLineSegment(sketch, "E59.0.88", {"start": v(685.54, 31.76) * mm, "end": v(533.2, 35.99) * mm});
            skLineSegment(sketch, "E59.0.89", {"start": v(533.2, 35.99) * mm, "end": v(533.06, 31.22) * mm});
            skLineSegment(sketch, "E59.0.90", {"start": v(533.06, 31.22) * mm, "end": v(464.46, 33.12) * mm});
            skLineSegment(sketch, "E59.0.91", {"start": v(464.46, 33.12) * mm, "end": v(464.32, 28.35) * mm});
            skLineSegment(sketch, "E59.0.92", {"start": v(464.32, 28.35) * mm, "end": v(468.75, 28.22) * mm});
            skLineSegment(sketch, "E59.0.93", {"start": v(468.75, 28.22) * mm, "end": v(468.7, 26.2) * mm});
            skLineSegment(sketch, "E59.0.94", {"start": v(468.7, 26.2) * mm, "end": v(466.48, 26.26) * mm});
            skLineSegment(sketch, "E59.0.95", {"start": v(466.48, 26.26) * mm, "end": v(466.33, 21.18) * mm});
            skLineSegment(sketch, "E59.0.96", {"start": v(466.33, 21.18) * mm, "end": v(464.13, 21.24) * mm});
            skLineSegment(sketch, "E59.0.97", {"start": v(464.13, 21.24) * mm, "end": v(463.99, 16.31) * mm});
            skLineSegment(sketch, "E59.0.98", {"start": v(463.99, 16.31) * mm, "end": v(461.44, 16.38) * mm});
            skLineSegment(sketch, "E59.0.99", {"start": v(461.44, 16.38) * mm, "end": v(458.89, 16.45) * mm});
            skLineSegment(sketch, "E59.0.100", {"start": v(458.89, 16.45) * mm, "end": v(459.02, 21.38) * mm});
            skLineSegment(sketch, "E59.0.101", {"start": v(459.02, 21.38) * mm, "end": v(456.81, 21.44) * mm});
            skLineSegment(sketch, "E59.0.102", {"start": v(456.81, 21.44) * mm, "end": v(456.95, 26.52) * mm});
            skLineSegment(sketch, "E59.0.103", {"start": v(456.95, 26.52) * mm, "end": v(454.73, 26.58) * mm});
            skLineSegment(sketch, "E59.0.104", {"start": v(454.73, 26.58) * mm, "end": v(454.79, 28.61) * mm});
            skLineSegment(sketch, "E59.0.105", {"start": v(454.79, 28.61) * mm, "end": v(459.22, 28.49) * mm});
            skLineSegment(sketch, "E59.0.106", {"start": v(459.22, 28.49) * mm, "end": v(459.35, 33.26) * mm});
            skLineSegment(sketch, "E59.0.107", {"start": v(459.35, 33.26) * mm, "end": v(380.72, 35.45) * mm});
            skLineSegment(sketch, "E59.0.108", {"start": v(380.72, 35.45) * mm, "end": v(380.85, 40.22) * mm});
            skLineSegment(sketch, "E59.0.109", {"start": v(380.85, 40.22) * mm, "end": v(228.51, 44.45) * mm});
            skLineSegment(sketch, "E59.0.110", {"start": v(228.51, 44.45) * mm, "end": v(228.38, 39.68) * mm});
            skLineSegment(sketch, "E59.0.111", {"start": v(228.38, 39.68) * mm, "end": v(159.77, 41.58) * mm});
            skLineSegment(sketch, "E59.0.112", {"start": v(159.77, 41.58) * mm, "end": v(159.64, 36.81) * mm});
            skLineSegment(sketch, "E59.0.113", {"start": v(159.64, 36.81) * mm, "end": v(164.07, 36.69) * mm});
            skLineSegment(sketch, "E59.0.114", {"start": v(164.07, 36.69) * mm, "end": v(164.02, 34.66) * mm});
            skLineSegment(sketch, "E59.0.115", {"start": v(164.02, 34.66) * mm, "end": v(161.8, 34.72) * mm});
            skLineSegment(sketch, "E59.0.116", {"start": v(161.8, 34.72) * mm, "end": v(161.65, 29.64) * mm});
            skLineSegment(sketch, "E59.0.117", {"start": v(161.65, 29.64) * mm, "end": v(159.44, 29.7) * mm});
            skLineSegment(sketch, "E59.0.118", {"start": v(159.44, 29.7) * mm, "end": v(159.3, 24.78) * mm});
            skLineSegment(sketch, "E59.0.119", {"start": v(159.3, 24.78) * mm, "end": v(156.75, 24.85) * mm});
            skLineSegment(sketch, "E59.0.120", {"start": v(156.75, 24.85) * mm, "end": v(154.2, 24.92) * mm});
            skLineSegment(sketch, "E59.0.121", {"start": v(154.2, 24.92) * mm, "end": v(154.34, 29.84) * mm});
            skLineSegment(sketch, "E59.0.122", {"start": v(154.34, 29.84) * mm, "end": v(152.13, 29.9) * mm});
            skLineSegment(sketch, "E59.0.123", {"start": v(152.13, 29.9) * mm, "end": v(152.27, 34.98) * mm});
            skLineSegment(sketch, "E59.0.124", {"start": v(152.27, 34.98) * mm, "end": v(150.05, 35.05) * mm});
            skLineSegment(sketch, "E59.0.125", {"start": v(150.05, 35.05) * mm, "end": v(150.1, 37.08) * mm});
            skLineSegment(sketch, "E59.0.126", {"start": v(150.1, 37.08) * mm, "end": v(154.54, 36.95) * mm});
            skLineSegment(sketch, "E59.0.127", {"start": v(154.54, 36.95) * mm, "end": v(154.67, 41.73) * mm});
            skLineSegment(sketch, "E59.0.128", {"start": v(154.67, 41.73) * mm, "end": v(76.04, 43.91) * mm});
            skLineSegment(sketch, "E59.0.129", {"start": v(76.04, 43.91) * mm, "end": v(76.17, 48.68) * mm});
            skCircle(sketch, "E60.0", {"center": v(914.4, 0) * mm, "radius": 3.18 * mm});
            skCircle(sketch, "E61.0", {"center": v(0, 0) * mm, "radius": 3.17 * mm});
            skSolve(sketch);
        }
        {
            var Q0;
            Q0 = qSketchRegion(id + "F6", true);
            extrude(context, id + "F7", {"entities" : qUnion([Q0]), "depth" : (getVariable(context, 'thick')) * mm});
        }
    });
